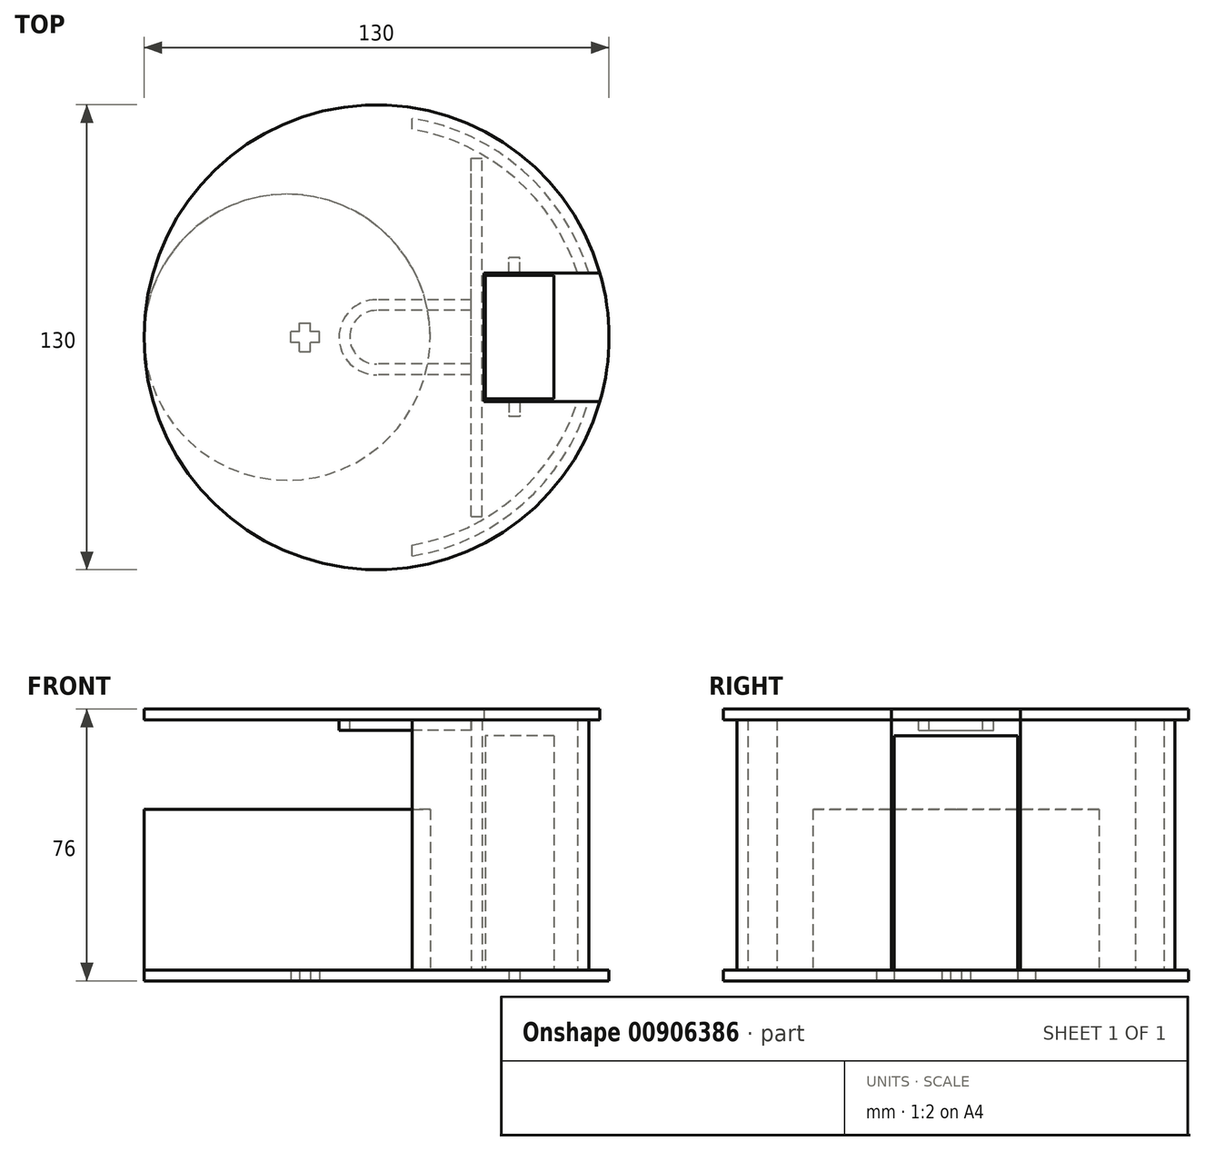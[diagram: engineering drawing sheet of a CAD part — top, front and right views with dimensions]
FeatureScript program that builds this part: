
annotation { "Feature Type Name" : "Feature", "Feature Type Description" : "" }
export const myFeature = defineFeature(function(context is Context, id is Id, definition is map)
    precondition{}
    {
        {
            var Q0;
            Q0=qCreatedBy(makeId("Top.planeOp"),FACE);
            var sketch = newSketch(context, id + "F0", { "sketchPlane" : qUnion([Q0])});
            skLineSegment(sketch, "E0.bottom", {"start": v(9.6, -17.25) * mm, "end": v(-9.6, -17.25) * mm});
            skLineSegment(sketch, "E0.top", {"start": v(9.6, 17.25) * mm, "end": v(-9.6, 17.25) * mm});
            skLineSegment(sketch, "E0.left", {"start": v(9.6, -17.25) * mm, "end": v(9.6, 17.25) * mm});
            skLineSegment(sketch, "E0.right", {"start": v(-9.6, -17.25) * mm, "end": v(-9.6, 17.25) * mm});
            skPoint(sketch, "E0.middle", {"position": v(0, 0) * mm});
            skSolve(sketch);
        }
        {
            var Q0;
            Q0 = qSketchRegion(id + "F0", true);
            extrude(context, id + "F1", {"entities" : qUnion([Q0]), "depth" : 68.5 * mm, "offsetDistance" : 25 * mm});
        }
        {
            var Q0;
            Q0=qCreatedBy(makeId("Top.planeOp"),FACE);
            var sketch = newSketch(context, id + "F2", { "sketchPlane" : qUnion([Q0])});
            skCircle(sketch, "E1", {"center": v(-40, 0) * mm, "radius": 65 * mm});
            skLineSegment(sketch, "E2.bottom", {"start": v(-61.5, -4) * mm, "end": v(-58.5, -4) * mm});
            skLineSegment(sketch, "E2.top", {"start": v(-61.5, 4) * mm, "end": v(-58.5, 4) * mm});
            skLineSegment(sketch, "E2.left", {"start": v(-61.5, -4) * mm, "end": v(-61.5, 4) * mm});
            skLineSegment(sketch, "E2.right", {"start": v(-58.5, -4) * mm, "end": v(-58.5, 4) * mm});
            skPoint(sketch, "E2.middle", {"position": v(-60, 0) * mm});
            skLineSegment(sketch, "E3.bottom", {"start": v(-56, -1.5) * mm, "end": v(-64, -1.5) * mm});
            skLineSegment(sketch, "E3.top", {"start": v(-56, 1.5) * mm, "end": v(-64, 1.5) * mm});
            skLineSegment(sketch, "E3.left", {"start": v(-56, -1.5) * mm, "end": v(-56, 1.5) * mm});
            skLineSegment(sketch, "E3.right", {"start": v(-64, -1.5) * mm, "end": v(-64, 1.5) * mm});
            skLineSegment(sketch, "E4.0", {"start": v(-9.6, -17.25) * mm, "end": v(-9.6, 17.25) * mm});
            skLineSegment(sketch, "E5.0", {"start": v(9.6, -17.25) * mm, "end": v(-9.6, -17.25) * mm});
            skLineSegment(sketch, "E6.bottom", {"start": v(0, -17.25) * mm, "end": v(-3, -17.25) * mm});
            skLineSegment(sketch, "E6.top", {"start": v(0, -22.25) * mm, "end": v(-3, -22.25) * mm});
            skLineSegment(sketch, "E6.left", {"start": v(0, -17.25) * mm, "end": v(0, -22.25) * mm});
            skLineSegment(sketch, "E6.right", {"start": v(-3, -17.25) * mm, "end": v(-3, -22.25) * mm});
            skLineSegment(sketch, "E7.0", {"start": v(9.6, 17.25) * mm, "end": v(-9.6, 17.25) * mm});
            skLineSegment(sketch, "E8.bottom", {"start": v(0, 17.25) * mm, "end": v(-3, 17.25) * mm});
            skLineSegment(sketch, "E8.top", {"start": v(0, 22.25) * mm, "end": v(-3, 22.25) * mm});
            skLineSegment(sketch, "E8.left", {"start": v(0, 17.25) * mm, "end": v(0, 22.25) * mm});
            skLineSegment(sketch, "E8.right", {"start": v(-3, 17.25) * mm, "end": v(-3, 22.25) * mm});
            skLineSegment(sketch, "E9", {"start": v(-12, 0) * mm, "end": v(-12, -53.3) * mm});
            skLineSegment(sketch, "E10.bottom", {"start": v(-12, -10) * mm, "end": v(-15, -10) * mm});
            skLineSegment(sketch, "E10.top", {"start": v(-12, -15) * mm, "end": v(-15, -15) * mm});
            skLineSegment(sketch, "E10.left", {"start": v(-12, -10) * mm, "end": v(-12, -15) * mm});
            skLineSegment(sketch, "E10.right", {"start": v(-15, -10) * mm, "end": v(-15, -15) * mm});
            skLineSegment(sketch, "E11", {"start": v(-30, 51.07) * mm, "end": v(-30, -54.7) * mm});
            skSolve(sketch);
        }
        {
            var Q0;
            Q0=makeQuery(id+"F2.imprint","IMPRINT",FACE,{"disambiguationData":[TD([[makeQuery(id+"F2.imprint","IMPRINT",EDGE,{"derivedFrom":sQuery(id+"F2.wireOp",EDGE,"7785a79c-8448-4c3b-9289-c4d7518b2b14.0")}),1.0]])]});
            var Q1;
            Q1=makeQuery(id+"F2.imprint","IMPRINT",FACE,{"disambiguationData":[TD([[makeQuery(id+"F2.imprint","IMPRINT",EDGE,{"derivedFrom":sQuery(id+"F2.wireOp",EDGE,"E1")}),1.0]])]});
            var Q2;
            Q2=makeQuery(id+"F2.imprint","IMPRINT",FACE,{"disambiguationData":[TD([[makeQuery(id+"F2.imprint","IMPRINT",EDGE,{"derivedFrom":sQuery(id+"F2.wireOp",EDGE,"E10.bottom")}),1.0]])]});
            extrude(context, id + "F3", {"entities" : qUnion([Q0, Q1, Q2]), "operationType" : NewBodyOperationType.ADD, "depth" : 3 * mm, "offsetDistance" : 25 * mm});
        }
        {
            var Q0;
            Q0=makeQuery(id+"F3.opExtrude","CAP_FACE",FACE,{"disambiguationData":[OSD([sQuery(id+"F2.wireOp",EDGE,"E1"),sQuery(id+"F2.wireOp",EDGE,"E2.bottom"),sQuery(id+"F2.wireOp",EDGE,"E2.top"),sQuery(id+"F2.wireOp",EDGE,"E2.left"),sQuery(id+"F2.wireOp",EDGE,"E2.right"),sQuery(id+"F2.wireOp",EDGE,"E3.bottom"),sQuery(id+"F2.wireOp",EDGE,"E3.top"),sQuery(id+"F2.wireOp",EDGE,"E3.left"),sQuery(id+"F2.wireOp",EDGE,"E3.right")])],"isStart":false});
            var sketch = newSketch(context, id + "F4", { "sketchPlane" : qUnion([Q0])});
            skCircle(sketch, "E12", {"center": v(-65, 0) * mm, "radius": 40 * mm});
            skSolve(sketch);
        }
        {
            var Q0;
            Q0 = qSketchRegion(id + "F4", true);
            extrude(context, id + "F5", {"entities" : qUnion([Q0]), "operationType" : NewBodyOperationType.ADD, "depth" : 45 * mm, "offsetDistance" : 25 * mm});
        }
        {
            var Q0;
            Q0=makeQuery(id+"F3.opExtrude","CAP_FACE",FACE,{"disambiguationData":[OSD([sQuery(id+"F2.wireOp",EDGE,"E1"),sQuery(id+"F2.wireOp",EDGE,"E2.bottom"),sQuery(id+"F2.wireOp",EDGE,"E2.top"),sQuery(id+"F2.wireOp",EDGE,"E2.left"),sQuery(id+"F2.wireOp",EDGE,"E2.right"),sQuery(id+"F2.wireOp",EDGE,"E3.bottom"),sQuery(id+"F2.wireOp",EDGE,"E3.top"),sQuery(id+"F2.wireOp",EDGE,"E3.left"),sQuery(id+"F2.wireOp",EDGE,"E3.right")])],"isStart":false});
            var sketch = newSketch(context, id + "F6", { "sketchPlane" : qUnion([Q0])});
            skLineSegment(sketch, "E13.bottom", {"start": v(-110, -80.24) * mm, "end": v(-30, -80.24) * mm, "construction": true});
            skLineSegment(sketch, "E13.top", {"start": v(-110, 80.24) * mm, "end": v(-30, 80.24) * mm, "construction": true});
            skLineSegment(sketch, "E13.left", {"start": v(-110, -80.24) * mm, "end": v(-110, 80.24) * mm, "construction": true});
            skLineSegment(sketch, "E13.right", {"start": v(-30, -80.24) * mm, "end": v(-30, -61.19) * mm, "construction": true});
            skPoint(sketch, "E13.middle", {"position": v(-70, 0) * mm});
            skLineSegment(sketch, "E14", {"start": v(-30, 61.19) * mm, "end": v(-30, 80.24) * mm, "construction": true});
            skLineSegment(sketch, "E15", {"start": v(-30, 58.15) * mm, "end": v(-30, 61.19) * mm});
            skLineSegment(sketch, "E16", {"start": v(-30, -58.15) * mm, "end": v(-30, 58.15) * mm});
            skLineSegment(sketch, "E17", {"start": v(-30, -61.19) * mm, "end": v(-30, -58.15) * mm});
            skArc(sketch, "E18", {"start": v(-30, 58.15) * mm, "mid": v(-99, 0) * mm, "end": v(-30, -58.15) * mm, "construction": true});
            skArc(sketch, "E19", {"start": v(-30, -58.15) * mm, "mid": v(-1.3, -44.53) * mm, "end": v(16.19, -18) * mm});
            skArc(sketch, "E20", {"start": v(-30, 61.19) * mm, "mid": v(-102, 0) * mm, "end": v(-30, -61.19) * mm, "construction": true});
            skArc(sketch, "E21", {"start": v(-30, -61.19) * mm, "mid": v(0.84, -46.65) * mm, "end": v(19.33, -18) * mm});
            skLineSegment(sketch, "E22.bottom", {"start": v(36.72, -18) * mm, "end": v(19.33, -18) * mm});
            skLineSegment(sketch, "E22.top", {"start": v(36.72, 18) * mm, "end": v(19.33, 18) * mm});
            skLineSegment(sketch, "E22.left", {"start": v(36.72, -18) * mm, "end": v(36.72, 18) * mm});
            skLineSegment(sketch, "E22.right", {"start": v(-23.28, -18) * mm, "end": v(-23.28, 18) * mm});
            skPoint(sketch, "E22.middle", {"position": v(6.72, 0) * mm});
            skArc(sketch, "E23", {"start": v(16.19, 18) * mm, "mid": v(-1.3, 44.53) * mm, "end": v(-30, 58.15) * mm});
            skArc(sketch, "E24", {"start": v(16.19, -18) * mm, "mid": v(19, 0) * mm, "end": v(16.19, 18) * mm});
            skLineSegment(sketch, "E25", {"start": v(19.33, -18) * mm, "end": v(16.19, -18) * mm});
            skArc(sketch, "E26", {"start": v(19.33, 18) * mm, "mid": v(0.84, 46.65) * mm, "end": v(-30, 61.19) * mm});
            skLineSegment(sketch, "E27", {"start": v(16.19, -18) * mm, "end": v(16.19, -18) * mm});
            skLineSegment(sketch, "E28", {"start": v(16.19, -18) * mm, "end": v(-23.28, -18) * mm});
            skArc(sketch, "E29", {"start": v(19.33, -18) * mm, "mid": v(22, 0) * mm, "end": v(19.33, 18) * mm});
            skLineSegment(sketch, "E30", {"start": v(16.19, 18) * mm, "end": v(-23.28, 18) * mm});
            skLineSegment(sketch, "E31", {"start": v(19.33, 18) * mm, "end": v(16.19, 18) * mm});
            skLineSegment(sketch, "E32.bottom", {"start": v(-13.5, -50.12) * mm, "end": v(-10.5, -50.12) * mm});
            skLineSegment(sketch, "E32.top", {"start": v(-13.5, 50.12) * mm, "end": v(-10.5, 50.12) * mm});
            skLineSegment(sketch, "E32.left", {"start": v(-13.5, -50.12) * mm, "end": v(-13.5, 50.12) * mm});
            skLineSegment(sketch, "E32.right", {"start": v(-10.5, -50.12) * mm, "end": v(-10.5, 50.12) * mm});
            skPoint(sketch, "E32.middle", {"position": v(-12, 0) * mm});
            skPoint(sketch, "E32.middle.positionSnap0", {"position": v(-30, 0) * mm});
            skPoint(sketch, "E32.centerSnap0", {"position": v(-30, 0) * mm});
            skCircle(sketch, "E33.0", {"center": v(-40, 0) * mm, "radius": 65 * mm});
            skLineSegment(sketch, "E33.1", {"start": v(-61.5, -4) * mm, "end": v(-58.5, -4) * mm});
            skLineSegment(sketch, "E33.2", {"start": v(-61.5, 4) * mm, "end": v(-58.5, 4) * mm});
            skLineSegment(sketch, "E33.3", {"start": v(-61.5, -4) * mm, "end": v(-61.5, 4) * mm});
            skLineSegment(sketch, "E33.4", {"start": v(-58.5, -4) * mm, "end": v(-58.5, 4) * mm});
            skPoint(sketch, "E33.5", {"position": v(-60, 0) * mm});
            skLineSegment(sketch, "E33.6", {"start": v(-56, -1.5) * mm, "end": v(-64, -1.5) * mm});
            skLineSegment(sketch, "E33.7", {"start": v(-56, 1.5) * mm, "end": v(-64, 1.5) * mm});
            skLineSegment(sketch, "E33.8", {"start": v(-56, -1.5) * mm, "end": v(-56, 1.5) * mm});
            skLineSegment(sketch, "E33.9", {"start": v(-64, -1.5) * mm, "end": v(-64, 1.5) * mm});
            skPoint(sketch, "E33.10", {"position": v(-60, 0) * mm});
            skLineSegment(sketch, "E33.11", {"start": v(-9.6, -17.25) * mm, "end": v(-9.6, 17.25) * mm});
            skLineSegment(sketch, "E33.12", {"start": v(9.6, -17.25) * mm, "end": v(-9.6, -17.25) * mm});
            skLineSegment(sketch, "E33.13", {"start": v(0, -17.25) * mm, "end": v(-3, -17.25) * mm});
            skLineSegment(sketch, "E33.14", {"start": v(0, -22.25) * mm, "end": v(-3, -22.25) * mm});
            skLineSegment(sketch, "E33.15", {"start": v(0, -17.25) * mm, "end": v(0, -22.25) * mm});
            skLineSegment(sketch, "E33.16", {"start": v(-3, -17.25) * mm, "end": v(-3, -22.25) * mm});
            skLineSegment(sketch, "E33.17", {"start": v(9.6, 17.25) * mm, "end": v(-9.6, 17.25) * mm});
            skLineSegment(sketch, "E33.18", {"start": v(0, 17.25) * mm, "end": v(-3, 17.25) * mm});
            skLineSegment(sketch, "E33.19", {"start": v(0, 22.25) * mm, "end": v(-3, 22.25) * mm});
            skLineSegment(sketch, "E33.20", {"start": v(0, 17.25) * mm, "end": v(0, 22.25) * mm});
            skLineSegment(sketch, "E33.21", {"start": v(-3, 17.25) * mm, "end": v(-3, 22.25) * mm});
            skLineSegment(sketch, "E33.22", {"start": v(-12, 0) * mm, "end": v(-12, -53.3) * mm, "construction": true});
            skLineSegment(sketch, "E33.23", {"start": v(-12, -10) * mm, "end": v(-15, -10) * mm, "construction": true});
            skLineSegment(sketch, "E33.24", {"start": v(-12, -15) * mm, "end": v(-15, -15) * mm, "construction": true});
            skLineSegment(sketch, "E33.25", {"start": v(-12, -10) * mm, "end": v(-12, -15) * mm});
            skLineSegment(sketch, "E33.26", {"start": v(-15, -10) * mm, "end": v(-15, -15) * mm, "construction": true});
            skSolve(sketch);
        }
        {
            var Q0;
            {var subQ0=sQuery(id+"F6.wireOp",EDGE,"E32.right");var subQ1=sQuery(id+"F6.wireOp",EDGE,"E28");var subQ2=makeQuery(id+"F6.imprint","INTERSECT",VERTEX,{"derivedFrom":[subQ1,subQ0]});Q0=makeQuery(id+"F6.imprint","IMPRINT",FACE,{"disambiguationData":[TD([[makeQuery(id+"F6.imprint","IMPRINT",EDGE,{"disambiguationData":[TD([[subQ2,-1.0]])],"derivedFrom":subQ1}),-1.0]])]});}
            var Q1;
            {var subQ5=sQuery(id+"F6.wireOp",EDGE,"E32.top");Q1=makeQuery(id+"F6.imprint","IMPRINT",FACE,{"disambiguationData":[TD([[makeQuery(id+"F6.imprint","IMPRINT",EDGE,{"derivedFrom":subQ5}),-1.0]])]});}
            var Q2;
            {var subQ5=sQuery(id+"F6.wireOp",EDGE,"E32.bottom");Q2=makeQuery(id+"F6.imprint","IMPRINT",FACE,{"disambiguationData":[TD([[makeQuery(id+"F6.imprint","IMPRINT",EDGE,{"derivedFrom":subQ5}),1.0]])]});}
            var Q3;
            Q3=makeQuery(id+"F6.imprint","IMPRINT",FACE,{"disambiguationData":[TD([[makeQuery(id+"F6.imprint","IMPRINT",EDGE,{"derivedFrom":sQuery(id+"F6.wireOp",EDGE,"E17")}),-1.0]])]});
            var Q4;
            Q4=makeQuery(id+"F6.imprint","IMPRINT",FACE,{"disambiguationData":[TD([[makeQuery(id+"F6.imprint","IMPRINT",EDGE,{"derivedFrom":sQuery(id+"F6.wireOp",EDGE,"E15")}),-1.0]])]});
            extrude(context, id + "F7", {"entities" : qUnion([Q0, Q1, Q2, Q3, Q4]), "operationType" : NewBodyOperationType.ADD, "depth" : 70 * mm, "offsetDistance" : 25 * mm});
        }
        {
            var Q0;
            Q0=sQuery(id+"F6.wireOp",EDGE,"E24");
            var Q1;
            Q1=sQuery(id+"F6.wireOp",EDGE,"E29");
            var Q2;
            Q2=sQuery(id+"F6.wireOp",EDGE,"E31");
            var Q3;
            Q3=sQuery(id+"F6.wireOp",EDGE,"E25");
            extrude(context, id + "F8", {"bodyType" : ToolBodyType.SURFACE, "surfaceEntities" : qUnion([Q0, Q1, Q2, Q3]), "depth" : 90 * mm, "offsetDistance" : 25 * mm});
        }
        {
            var Q0;
            Q0=makeQuery(id+"F3.opExtrude","CAP_FACE",FACE,{"disambiguationData":[OSD([sQuery(id+"F2.wireOp",EDGE,"E1"),sQuery(id+"F2.wireOp",EDGE,"E2.bottom"),sQuery(id+"F2.wireOp",EDGE,"E2.top"),sQuery(id+"F2.wireOp",EDGE,"E2.left"),sQuery(id+"F2.wireOp",EDGE,"E2.right"),sQuery(id+"F2.wireOp",EDGE,"E3.bottom"),sQuery(id+"F2.wireOp",EDGE,"E3.top"),sQuery(id+"F2.wireOp",EDGE,"E3.left"),sQuery(id+"F2.wireOp",EDGE,"E3.right")])],"isStart":false});
            cPlane(context, id + "F9", {"entities" : qUnion([Q0]), "cplaneType" : CPlaneType.OFFSET, "offset" : 70 * mm, "width" : 150 * mm, "height" : 150 * mm});
        }
        {
            var Q0;
            Q0=qCreatedBy(id+"F9.planeOp",FACE);
            var sketch = newSketch(context, id + "F10", { "sketchPlane" : qUnion([Q0])});
            skLineSegment(sketch, "E34.bottom", {"start": v(30, -18) * mm, "end": v(-10, -18) * mm});
            skLineSegment(sketch, "E34.top", {"start": v(30, 18) * mm, "end": v(-10, 18) * mm});
            skLineSegment(sketch, "E34.left", {"start": v(30, -18) * mm, "end": v(30, 18) * mm});
            skLineSegment(sketch, "E34.right", {"start": v(-10, -18) * mm, "end": v(-10, 18) * mm});
            skPoint(sketch, "E34.middle", {"position": v(10, 0) * mm});
            skArc(sketch, "E35", {"start": v(22.46, 18) * mm, "mid": v(-105, 0) * mm, "end": v(22.46, -18) * mm});
            skArc(sketch, "E36", {"start": v(22.46, -18) * mm, "mid": v(25, 0) * mm, "end": v(22.46, 18) * mm});
            skSolve(sketch);
        }
        {
            var Q0;
            {var subQ0=sQuery(id+"F10.wireOp",EDGE,"E34.right");Q0=makeQuery(id+"F10.imprint","IMPRINT",FACE,{"disambiguationData":[TD([[makeQuery(id+"F10.imprint","IMPRINT",EDGE,{"derivedFrom":subQ0}),1.0]])]});}
            extrude(context, id + "F11", {"entities" : qUnion([Q0]), "operationType" : NewBodyOperationType.ADD, "depth" : 3 * mm, "offsetDistance" : 25 * mm});
        }
        {
            var Q0;
            Q0=makeQuery(id+"F11.opExtrude","CAP_FACE",FACE,{"disambiguationData":[OSD([sQuery(id+"F10.wireOp",EDGE,"E34.bottom"),sQuery(id+"F10.wireOp",EDGE,"E34.top"),sQuery(id+"F10.wireOp",EDGE,"E34.right"),sQuery(id+"F10.wireOp",EDGE,"E35")])],"isStart":true});
            var sketch = newSketch(context, id + "F12", { "sketchPlane" : qUnion([Q0])});
            skLineSegment(sketch, "E37.bottom", {"start": v(-13.5, -7.5) * mm, "end": v(-40, -7.5) * mm});
            skLineSegment(sketch, "E37.top", {"start": v(-13.5, 7.5) * mm, "end": v(-40, 7.5) * mm});
            skLineSegment(sketch, "E37.left", {"start": v(-13.5, -7.5) * mm, "end": v(-13.5, -7.5) * mm});
            skLineSegment(sketch, "E37.right", {"start": v(-40, -7.5) * mm, "end": v(-40, 7.5) * mm, "construction": true});
            skPoint(sketch, "E37.middle", {"position": v(-26.75, 0) * mm});
            skArc(sketch, "E38", {"start": v(-40, 7.5) * mm, "mid": v(-47.5, 0) * mm, "end": v(-40, -7.5) * mm});
            skArc(sketch, "E39", {"start": v(-40, -7.5) * mm, "mid": v(-32.5, 0) * mm, "end": v(-40, 7.5) * mm, "construction": true});
            skLineSegment(sketch, "E40.0", {"start": v(-13.5, -10.5) * mm, "end": v(-40, -10.5) * mm});
            skArc(sketch, "E40.1", {"start": v(-40, 10.5) * mm, "mid": v(-50.5, 0) * mm, "end": v(-40, -10.5) * mm});
            skLineSegment(sketch, "E40.2", {"start": v(-13.5, 10.5) * mm, "end": v(-13.5, 10.5) * mm});
            skLineSegment(sketch, "E41", {"start": v(-13.5, -7.5) * mm, "end": v(-13.5, 7.5) * mm});
            skLineSegment(sketch, "E42.0", {"start": v(-13.5, 50.12) * mm, "end": v(-13.5, 10.5) * mm});
            skLineSegment(sketch, "E43", {"start": v(-13.5, -10.5) * mm, "end": v(-13.5, -50.12) * mm});
            skLineSegment(sketch, "E44", {"start": v(-13.5, -7.5) * mm, "end": v(-13.5, -10.5) * mm});
            skLineSegment(sketch, "E45", {"start": v(-13.5, 7.5) * mm, "end": v(-13.5, -7.5) * mm});
            skLineSegment(sketch, "E46", {"start": v(-13.5, 10.5) * mm, "end": v(-40, 10.5) * mm});
            skLineSegment(sketch, "E47", {"start": v(-13.5, 10.5) * mm, "end": v(-13.5, 7.5) * mm});
            skSolve(sketch);
        }
        {
            var Q0;
            Q0=makeQuery(id+"F12.imprint","IMPRINT",FACE,{"disambiguationData":[TD([[makeQuery(id+"F12.imprint","IMPRINT",EDGE,{"derivedFrom":sQuery(id+"F12.wireOp",EDGE,"E37.bottom")}),1.0]])]});
            extrude(context, id + "F13", {"entities" : qUnion([Q0]), "operationType" : NewBodyOperationType.ADD, "depth" : 3 * mm, "offsetDistance" : 25 * mm});
        }
    });
